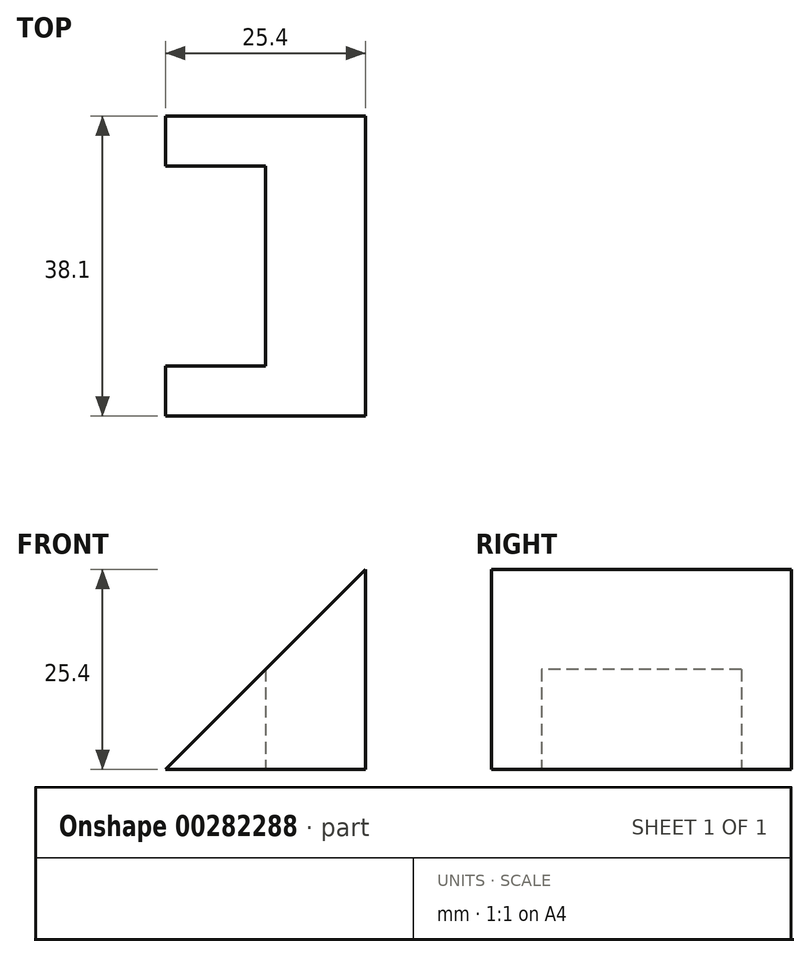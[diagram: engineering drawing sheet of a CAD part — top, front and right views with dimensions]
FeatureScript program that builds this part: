
annotation { "Feature Type Name" : "Feature", "Feature Type Description" : "" }
export const myFeature = defineFeature(function(context is Context, id is Id, definition is map)
    precondition{}
    {
        {
            var Q0;
            Q0=qCreatedBy(makeId("Front.planeOp"),FACE);
            var sketch = newSketch(context, id + "F0", { "sketchPlane" : qUnion([Q0])});
            skLineSegment(sketch, "E0", {"start": v(0, 0) * mm, "end": v(-25.4, 0) * mm});
            skLineSegment(sketch, "E1", {"start": v(-25.4, 0) * mm, "end": v(0, 25.4) * mm});
            skLineSegment(sketch, "E2", {"start": v(0, 25.4) * mm, "end": v(0, 0) * mm});
            skSolve(sketch);
        }
        {
            var Q0;
            Q0 = qSketchRegion(id + "F0", true);
            extrude(context, id + "F1", {"entities" : qUnion([Q0]), "depth" : 38.1 * mm});
        }
        {
            var Q0;
            Q0=makeQuery(id+"F1.opExtrude","SWEPT_FACE",FACE,{"disambiguationData":[OSD([sQuery(id+"F0.wireOp",EDGE,"E0")])]});
            var sketch = newSketch(context, id + "F2", { "sketchPlane" : qUnion([Q0])});
            skLineSegment(sketch, "E3.bottom", {"start": v(-25.4, 31.75) * mm, "end": v(-12.7, 31.75) * mm});
            skLineSegment(sketch, "E3.top", {"start": v(-25.4, 6.35) * mm, "end": v(-12.7, 6.35) * mm});
            skLineSegment(sketch, "E3.left", {"start": v(-25.4, 31.75) * mm, "end": v(-25.4, 6.35) * mm});
            skLineSegment(sketch, "E3.right", {"start": v(-12.7, 31.75) * mm, "end": v(-12.7, 6.35) * mm});
            skSolve(sketch);
        }
        {
            var Q0;
            Q0 = qSketchRegion(id + "F2", true);
            extrude(context, id + "F3", {"entities" : qUnion([Q0]), "operationType" : NewBodyOperationType.REMOVE, "oppositeDirection" : true, "depth" : 25.4 * mm});
        }
    });
